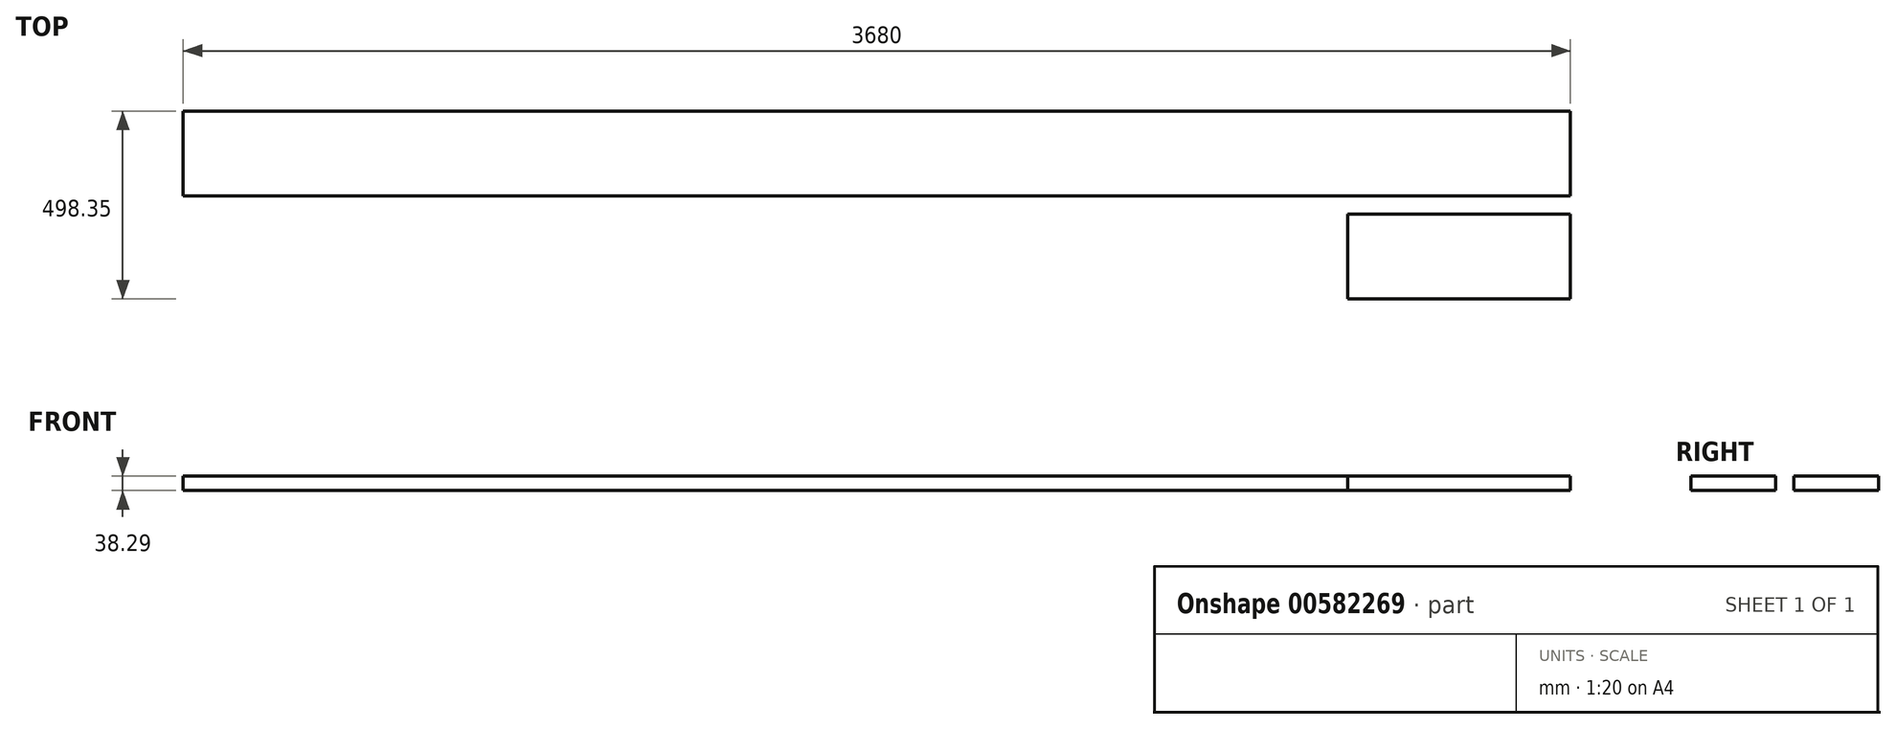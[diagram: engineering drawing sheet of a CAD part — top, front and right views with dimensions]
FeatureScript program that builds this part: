
annotation { "Feature Type Name" : "Feature", "Feature Type Description" : "" }
export const myFeature = defineFeature(function(context is Context, id is Id, definition is map)
    precondition{}
    {
        {
            var Q0;
            Q0=qCreatedBy(makeId("Right.planeOp"),FACE);
            var sketch = newSketch(context, id + "F0", { "sketchPlane" : qUnion([Q0])});
            skLineSegment(sketch, "E0.bottom", {"start": v(48.88, 19) * mm, "end": v(273.88, 19) * mm});
            skLineSegment(sketch, "E0.top", {"start": v(48.88, -19) * mm, "end": v(273.88, -19) * mm});
            skLineSegment(sketch, "E0.left", {"start": v(48.88, 19) * mm, "end": v(48.88, -19) * mm});
            skLineSegment(sketch, "E0.right", {"start": v(273.88, 19) * mm, "end": v(273.88, -19) * mm});
            skPoint(sketch, "E0.middle", {"position": v(161.38, 0) * mm});
            skLineSegment(sketch, "E1.bottom", {"start": v(-224.47, 18.7) * mm, "end": v(0.53, 18.7) * mm});
            skLineSegment(sketch, "E1.top", {"start": v(-224.47, -19.3) * mm, "end": v(0.53, -19.3) * mm});
            skLineSegment(sketch, "E1.left", {"start": v(-224.47, 18.7) * mm, "end": v(-224.47, -19.3) * mm});
            skLineSegment(sketch, "E1.right", {"start": v(0.53, 18.7) * mm, "end": v(0.53, -19.3) * mm});
            skPoint(sketch, "E1.middle", {"position": v(-111.97, -0.3) * mm});
            skSolve(sketch);
        }
        {
            var Q0;
            Q0=makeQuery(id+"F0.imprint","IMPRINT",FACE,{"disambiguationData":[TD([[makeQuery(id+"F0.imprint","IMPRINT",EDGE,{"derivedFrom":sQuery(id+"F0.wireOp",EDGE,"E0.bottom")}),-1.0]])]});
            extrude(context, id + "F1", {"entities" : qUnion([Q0]), "oppositeDirection" : true, "depth" : 3680 * mm, "offsetDistance" : 25 * mm});
        }
        {
            var Q0;
            Q0=makeQuery(id+"F0.imprint","IMPRINT",FACE,{"disambiguationData":[TD([[makeQuery(id+"F0.imprint","IMPRINT",EDGE,{"derivedFrom":sQuery(id+"F0.wireOp",EDGE,"E1.bottom")}),-1.0]])]});
            extrude(context, id + "F2", {"entities" : qUnion([Q0]), "oppositeDirection" : true, "depth" : 590 * mm, "offsetDistance" : 25 * mm});
        }
    });
